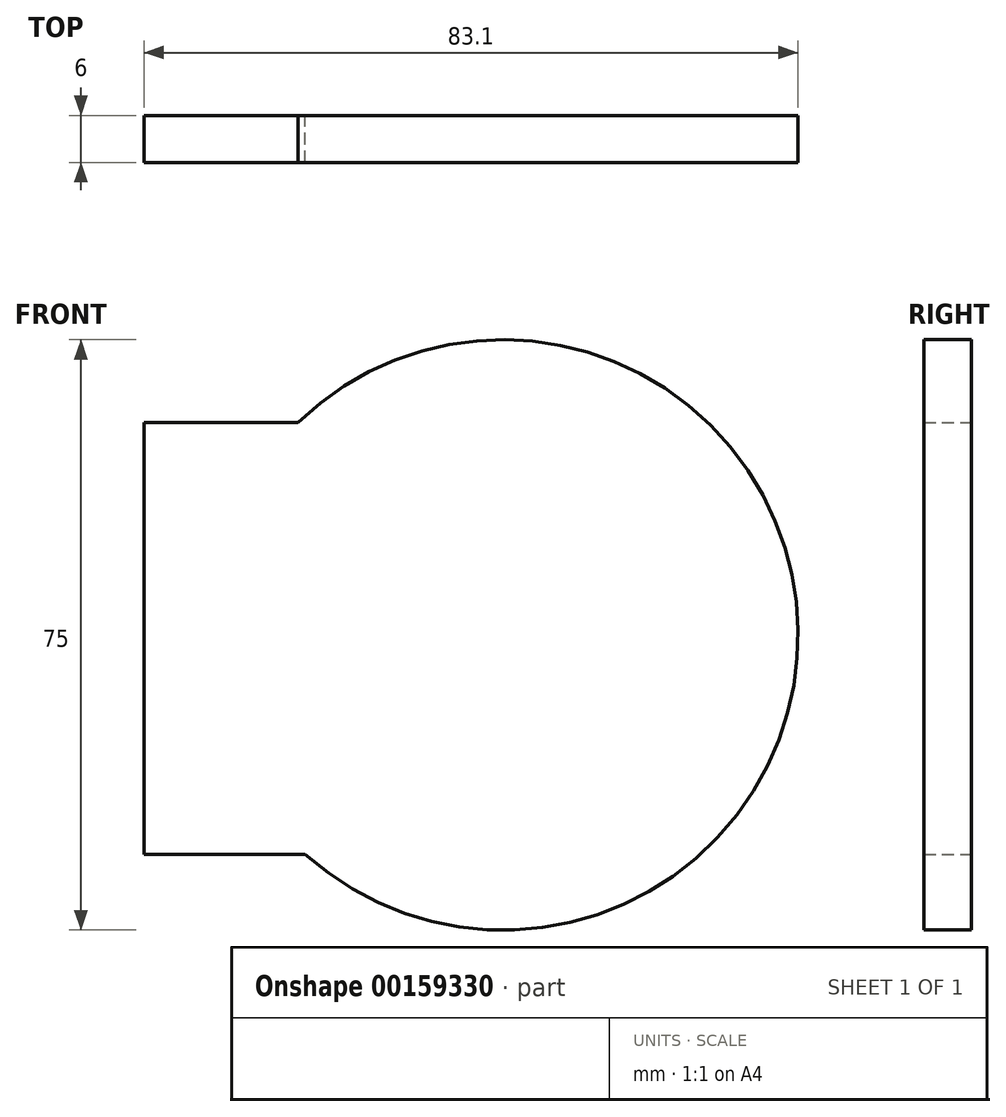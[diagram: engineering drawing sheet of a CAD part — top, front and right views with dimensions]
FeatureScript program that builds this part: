
annotation { "Feature Type Name" : "Feature", "Feature Type Description" : "" }
export const myFeature = defineFeature(function(context is Context, id is Id, definition is map)
    precondition{}
    {
        {
            var Q0;
            Q0=qCreatedBy(makeId("Front.planeOp"),FACE);
            var sketch = newSketch(context, id + "F0", { "sketchPlane" : qUnion([Q0])});
            skArc(sketch, "E0", {"start": v(-12.5, -27.86) * mm, "mid": v(50.1, 0.63) * mm, "end": v(-13.43, 27) * mm});
            skLineSegment(sketch, "E1", {"start": v(-13.43, 27) * mm, "end": v(-33, 27) * mm});
            skLineSegment(sketch, "E2", {"start": v(-33, 27) * mm, "end": v(-33, -27.86) * mm});
            skLineSegment(sketch, "E3", {"start": v(-33, -27.86) * mm, "end": v(-12.5, -27.86) * mm});
            skSolve(sketch);
        }
        {
            var Q0;
            Q0=qSketchRegion(id+"F0",true);
            extrude(context, id + "F1", {"entities" : qUnion([Q0]), "depth" : 6 * mm});
        }
    });
